# Revit family: 220-45 Heavy  Retract roof, 4 Sides, Blades Retracting to one side
name_source: partatom
category: Generic Models
revit_build: Autodesk Revit 2018 (Build: 20190510_1515(x64)
units: mm (PartAtom-declared; Revit-internal decimal feet)

## family parameters
Always vertical = Yes
Can host rebar = No
Cut with Voids When Loaded = No
Part Type = Normal
Room Calculation Point = No
Round Connector Dimension = Use Diameter
Shared = No
Work Plane-Based = No

## types (1)
- 220-45 Heavy  Retract roof, 4 Sides, Blades Retracting to one side
    220 45 HEAVY BLADE AND END CAP = PC COLOUR
    A = 2652 mm  [stored 8.70079 ft]
    ANGLE INPUT = 0.00°
    ANGLE LIMIT = 90.00°
    BLADE ANGLE = 0.00°
    BLADE PITCH = 1.30°
    BLADES SPACING = 0 mm  [stored 0 ft]
    BOX SECTION HEIGHT = 250 mm  [stored 0.82021 ft]
    BOX SECTION HEIGHT INPUT = 300 mm
    BOX SECTION THICKNESS = 3 mm  [stored 0.00984252 ft]
    BOX SECTION THICKNESS INPUT = 3 mm  [stored 0.00984252 ft]
    BOX SECTION WIDTH = 50 mm  [stored 0.164042 ft]
    BOX SECTION WIDTH INPUT = 50 mm  [stored 0.164042 ft]
    DETAIL OFFSET = 0 mm  [stored 0 ft]
    DETAIL OFFSET INPUT = 0 mm  [stored 0 ft]
    FLASHING INPUT = 0 mm  [stored 0 ft]
    GUTTER = PC COLOUR
    HEIGHT = 2200 mm
    HEIGHT LIMIT = 2200 mm
    M1 = 170 mm  [stored 0.557743 ft]
    NUMBER OF BLADES = 12
    O = 60 mm  [stored 0.19685 ft]
    PIVOT = 3000 mm  [stored 9.84252 ft]
    POST = PC COLOUR
    POST LENGTH AND WIDTH SIZE = 100 mm  [stored 0.328084 ft]
    POST LENGTH AND WIDTH SIZE INPUT = 100 mm  [stored 0.328084 ft]
    POST THICKNESS = 3 mm  [stored 0.00984252 ft]
    POST THICKNESS INPUT = 3 mm  [stored 0.00984252 ft]
    RETRACT FRAME = PC COLOUR
    SPACING INPUT = 60 mm  [stored 0.19685 ft]
    SPAN = 3000 mm  [stored 9.84252 ft]
    SPAN INPUT = 3000 mm  [stored 9.84252 ft]
    STACKED INPUT = 260 mm  [stored 0.853018 ft]
    WOOL PILE = WOOL pILE

note: [stored X ft] marks values corroborated as IEEE doubles in the binary element streams (Revit-internal decimal feet)

## geometry (parser evidence)
native form markers: Sweep x35
no freeform markers — native parametric forms only
